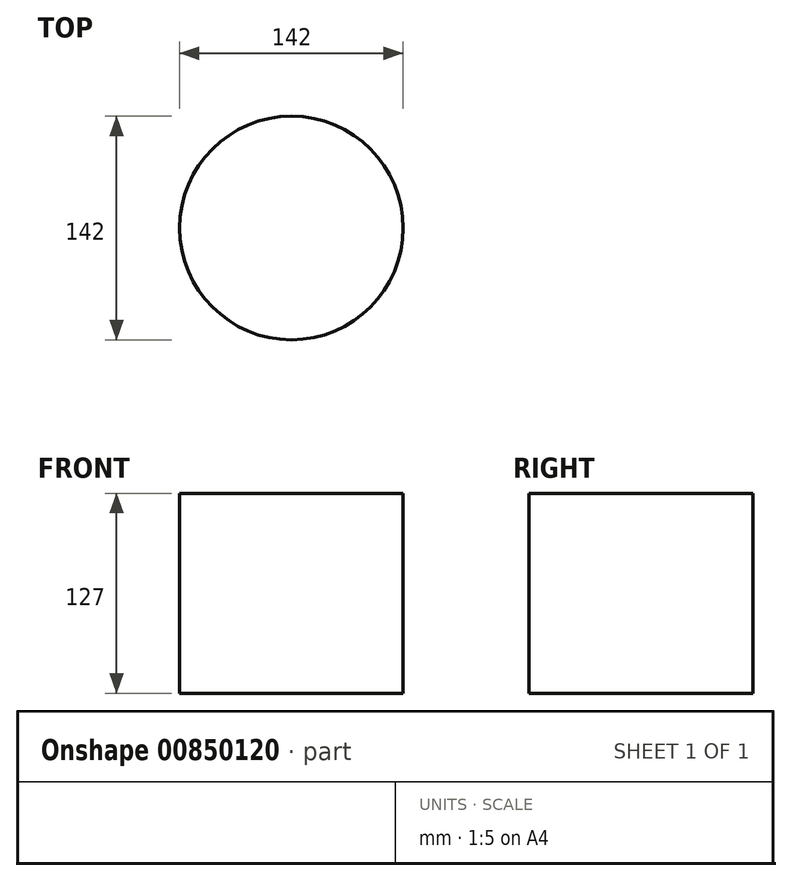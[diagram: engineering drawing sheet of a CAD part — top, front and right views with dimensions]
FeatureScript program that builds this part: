
annotation { "Feature Type Name" : "Feature", "Feature Type Description" : "" }
export const myFeature = defineFeature(function(context is Context, id is Id, definition is map)
    precondition{}
    {
        {
            var Q0;
            Q0=qCreatedBy(makeId("Top.planeOp"),FACE);
            var sketch = newSketch(context, id + "F0", { "sketchPlane" : qUnion([Q0])});
            skCircle(sketch, "E0", {"center": v(0, 0) * mm, "radius": 71 * mm});
            skSolve(sketch);
        }
        {
            var Q0;
            Q0=makeQuery(id+"F0.imprint","IMPRINT",FACE,{"disambiguationData":[TD([[makeQuery(id+"F0.imprint","IMPRINT",EDGE,{"derivedFrom":sQuery(id+"F0.wireOp",EDGE,"E0")}),1.0]])]});
            extrude(context, id + "F1", {"entities" : qUnion([Q0]), "depth" : 127 * mm, "offsetDistance" : 25.4 * mm});
        }
        {
            var Q0;
            Q0=qCreatedBy(makeId("Top.planeOp"),FACE);
            var sketch = newSketch(context, id + "F2", { "sketchPlane" : qUnion([Q0])});
            skCircle(sketch, "E1", {"center": v(0, 0) * mm, "radius": 64.09 * mm});
            skSolve(sketch);
        }
        {
            var Q0;
            Q0=sQuery(id+"F2.wireOp",EDGE,"E1");
            extrude(context, id + "F3", {"bodyType" : ToolBodyType.SURFACE, "surfaceEntities" : qUnion([Q0]), "depth" : -127 * mm, "offsetDistance" : 25.4 * mm});
        }
    });
